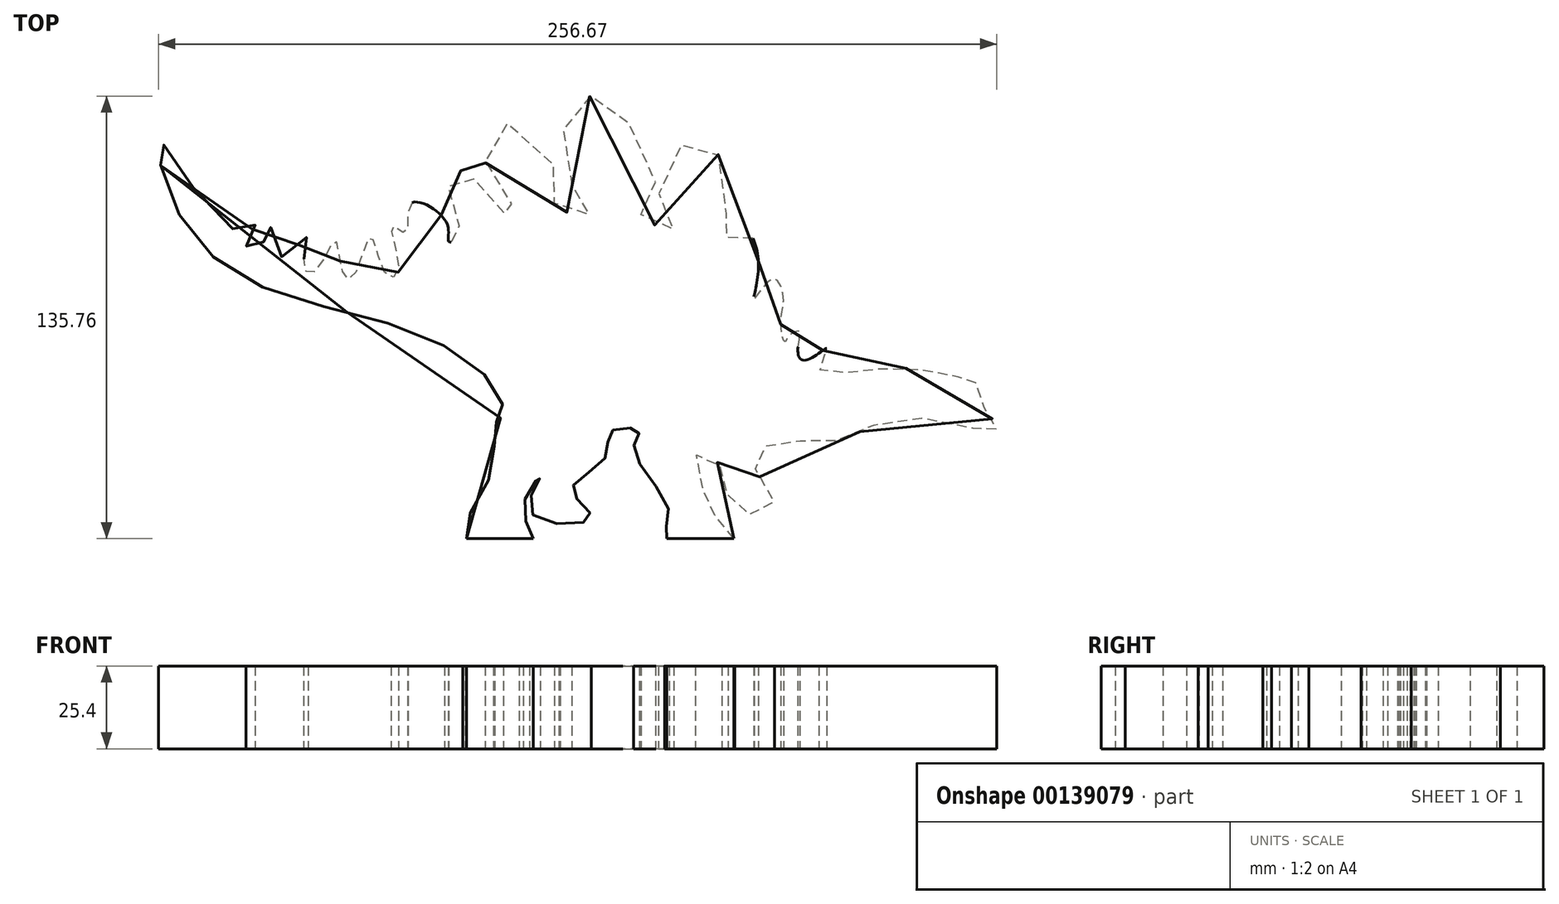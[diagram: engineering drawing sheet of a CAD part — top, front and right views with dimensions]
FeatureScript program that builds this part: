
annotation { "Feature Type Name" : "Feature", "Feature Type Description" : "" }
export const myFeature = defineFeature(function(context is Context, id is Id, definition is map)
    precondition{}
    {
        {
            var Q0;
            Q0=qCreatedBy(makeId("Top.planeOp"),FACE);
            var sketch = newSketch(context, id + "F0", { "sketchPlane" : qUnion([Q0])});
            skFitSpline(sketch, "E0", {"points": [v(-131.46, 14.43) * mm, v(-129.45, 0) * mm, v(-105.3, -27.44) * mm, v(-55.78, -42.74) * mm, v(-29.61, -60.05) * mm, v(-27.2, -68.9) * mm, v(-29.61, -72.12) * mm, v(-29.61, -82.6) * mm, v(-36.45, -97.89) * mm, v(-38.06, -106.75) * mm, v(-17.94, -108.76) * mm, v(-20.75, -97.08) * mm, v(-15.52, -87.82) * mm, v(-18.34, -98.7) * mm, v(0, -100.3) * mm, v(-5.86, -91.85) * mm, v(4.2, -82.19) * mm, v(6.22, -73.73) * mm, v(14.67, -73.73) * mm, v(13.06, -78.97) * mm, v(23.93, -98.7) * mm, v(23.16, -106.75) * mm, v(43.8, -106.75) * mm, v(38.06, -99.61) * mm, v(34.8, -93.06) * mm, v(32.38, -80.98) * mm, v(38.64, -83.28) * mm, v(41.21, -91.3) * mm, v(46.37, -98.75) * mm, v(56.12, -96.75) * mm, v(50.39, -85.29) * mm, v(52.4, -78.98) * mm, v(63.57, -76.69) * mm, v(77.07, -76.15) * mm, v(93.98, -69.7) * mm, v(119.34, -73.33) * mm, v(124.17, -73.33) * mm, v(122.56, -69.3) * mm, v(118.53, -62.87) * mm, v(117.33, -57.63) * mm, v(113.3, -57.23) * mm, v(100.02, -54.81) * mm, v(83.51, -55.22) * mm, v(75.06, -56.02) * mm, v(69.82, -54) * mm, v(72.24, -48.37) * mm, v(65.8, -52) * mm, v(63.38, -49.18) * mm, v(63.78, -43.14) * mm, v(60.56, -44.75) * mm, v(59.36, -46.36) * mm, v(58.15, -40.72) * mm, v(58.95, -32.67) * mm, v(55.73, -27.04) * mm, v(50.1, -33.08) * mm, v(51.3, -23.01) * mm, v(46.07, -11.74) * mm, v(40.44, -14.96) * mm, v(42.05, 0) * mm, v(32.38, 15.63) * mm, v(20.71, 0) * mm, v(25.14, -11.74) * mm, v(15.48, -7.71) * mm, v(19.5, 0) * mm, v(6.22, 26.5) * mm, v(-3.44, 27.3) * mm, v(-8.27, 5.97) * mm, v(0, -6.9) * mm, v(-10.69, -4.9) * mm, v(-9.88, 3.56) * mm, v(-28, 20.47) * mm, v(-29.61, 0) * mm, v(-21.96, -5.7) * mm, v(-29.2, -6.1) * mm, v(-38.87, 6.38) * mm, v(-44.5, -6.1) * mm, v(-38.47, -13.35) * mm, v(-43.3, -15.77) * mm, v(-44.1, -10.13) * mm, v(-55.37, -4.1) * mm, v(-56.58, -12.95) * mm, v(-61.01, -10.93) * mm, v(-59, -24.62) * mm, v(-62.62, -25.83) * mm, v(-67.45, -14.16) * mm, v(-73.09, -26.63) * mm, v(-75.9, -25.43) * mm, v(-78.32, -15.36) * mm, v(-84.76, -25.02) * mm, v(-87.98, -23.01) * mm, v(-86.77, -14.16) * mm, v(-95.23, -20.2) * mm, v(-98.45, -10.13) * mm, v(-102.07, -18.58) * mm, v(-105.7, -16.17) * mm, v(-102.88, -10.53) * mm, v(-109.72, -11.74) * mm, v(-131.46, 14.43) * mm]});
            skLineSegment(sketch, "E1", {"start": v(-57.08, -106.75) * mm, "end": v(-112.1, -94.74) * mm});
            skLineSegment(sketch, "E2", {"start": v(-49.34, -106.75) * mm, "end": v(79.33, -106.75) * mm});
            skSolve(sketch);
        }
        {
            var Q0;
            {var subQ0=sQuery(id+"F0.wireOp",EDGE,"E2");var subQ1=sQuery(id+"F0.wireOp",EDGE,"E0");var subQ2=makeQuery(id+"F0.imprint","INTERSECT",VERTEX,{"disambiguationData":[OD(2.0)],"derivedFrom":[subQ1,subQ0]});Q0=makeQuery(id+"F0.imprint","IMPRINT",FACE,{"disambiguationData":[TD([[makeQuery(id+"F0.imprint","IMPRINT",EDGE,{"disambiguationData":[TD([[subQ2,-1.0]])],"derivedFrom":subQ1}),1.0]])]});}
            extrude(context, id + "F1", {"entities" : qUnion([Q0]), "depth" : 25.4 * mm});
        }
    });
